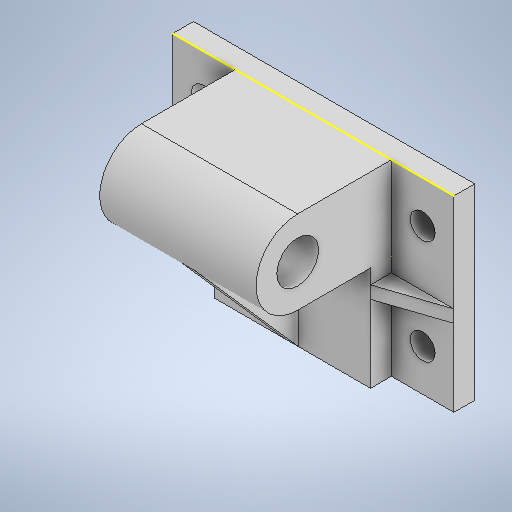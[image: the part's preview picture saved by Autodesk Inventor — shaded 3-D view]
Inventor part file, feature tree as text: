
AUTODESK INVENTOR PART (.ipt)
format: ipt  version: 2025.2 (Build 292293000, 293)  size: 348,672 bytes
history: native  units: in
note: dims shown in document units (in); Inventor stores cm internally (conversion verified against a paired STEP export)
features: sketch x11, extrude x5, rib x3, plane x2
ambient origin geometry x8: Origin, YZ Plane, XZ Plane, XY Plane, X Axis, Y Axis, Z Axis, Center Point
bodies: Solid1 (feature_tree)
feature tree (21):
  sketch  "Sketch1"  dims[d0=5.315in d1=3.5433in]
  extrude  "Extrusion1"  Depth=3.5433in
  extrude  "Extrusion2"  Depth=2.9528in
  extrude  "Extrusion3"  Depth=2.1654in
  sketch  "Sketch5"  dims[d10=0.3937in d11=0.0in d14=0.3937in d15=0.0in]
  plane  "Work Plane1"
  extrude  "Extrusion4"  Depth=1.9685in
  plane  "Work Plane2"
  rib  "Rib1"
  sketch  "Sketch8"  dims[d20=1.7717in]
  rib  "Rib2"
  rib  "Rib3"
  extrude  "Extrusion5"  Depth=0.3937in TaperAngle=0.0deg
  sketch  "Sketch2"  dims[d2=0.3937in d3=0.0in d4=2.9528in]
  sketch  "Sketch3"  dims[d5=3.5433in d6=2.1654in]
  sketch  "Sketch4"  dims[d8=0.3937in d9=1.9685in]
  sketch  "Sketch6"  dims[d16=1.9685in d17=0.0in]
  sketch  "Sketch7"  dims[d19=-1.4764in]
  sketch  "Sketch9"  dims[d21=1.7717in]
  sketch  "Sketch10"  dims[d22=0.7874in]
  sketch  "Sketch11"  dims[d23=0.7874in d24=2.9528in d25=0.0in d26=-0.1969in d27=0.0394in d28=0.2362in d29=0.0in d30=0.0in d31=0.0394in d32=0.0394in d33=0.0394in d34=0.2362in d35=0.0in d36=0.0in d37=0.0394in d38=0.0394in d39=0.0394in d40=0.2362in d41=0.0in d42=0.0in d43=0.0394in d44=0.0394in d45=0.4724in d46=0.5906in d47=0.7874in d48=0.4724in d49=0.4724in d50=0.4724in d51=0.5906in d52=0.5906in d53=0.5906in d54=0.7874in d55=0.7874in d56=0.7874in d57=0.0in d58=0.0in]
